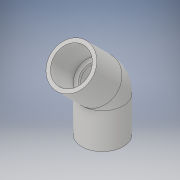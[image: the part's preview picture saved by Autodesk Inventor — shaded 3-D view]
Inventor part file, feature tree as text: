
AUTODESK INVENTOR PART (.ipt)
format: ipt  version: 2018 (Build 220112000, 112)  size: 171,520 bytes
history: native  units: in
note: dims shown in document units (in); Inventor stores cm internally (conversion verified against a paired STEP export)
features: sketch x10, extrude x6, plane x5, revolve x2, other x1
ambient origin geometry x8: Origin, YZ Plane, XZ Plane, XY Plane, X Axis, Y Axis, Z Axis, Center Point
bodies: Solid1 (feature_tree)
feature tree (24):
  extrude  "Extrusion1"  Depth=1.367in TaperAngle=0.0deg
  sketch  "Sketch2"  dims[d3=-0.3092in d4=1.367in d5=0.0in]
  plane  "Work Plane1"
  extrude  "Extrusion2"  Depth=1.367in TaperAngle=0.0deg
  extrude  "Extrusion3"  Depth=1.25in TaperAngle=0.0deg
  extrude  "Extrusion4"  Depth=1.25in TaperAngle=0.0deg
  plane  "Work Plane2"
  plane  "Work Plane3"
  revolve  "Revolution1"  Angle=45.0deg
  plane  "Work Plane4"
  sketch  "Sketch6"  dims[d15=-0.3092in d17=1.0in]
  plane  "Work Plane5"
  sketch  "Sketch8"  dims[d18=0.117in d19=0.0in d20=1.0in]
  extrude  "Extrusion5"  Depth=1.0in
  extrude  "Extrusion6"  Depth=1.0in
  other  "Work Axis1"
  revolve  "Revolution2"  [1 undecoded]
  sketch  "Sketch1"  dims[d0=1.605in d1=1.367in d2=0.0in]
  sketch  "Sketch3"  dims[d6=1.321in d7=1.25in d8=0.0in]
  sketch  "Sketch4"  dims[d9=1.321in d10=1.25in d11=0.0in]
  sketch  "Sketch5"  dims[d12=0.0in d13=0.0in d14=45.0deg]
  sketch  "Sketch9"  dims[d21=0.117in d22=0.0in d23=0.2749in]
  sketch  "Sketch10"
  sketch  "Sketch11"
note: 1 required parameter value undecoded (feature->parameter linkage not recoverable at this tier; creation-order binding heuristic only, values carry confidence <= 0.55)
